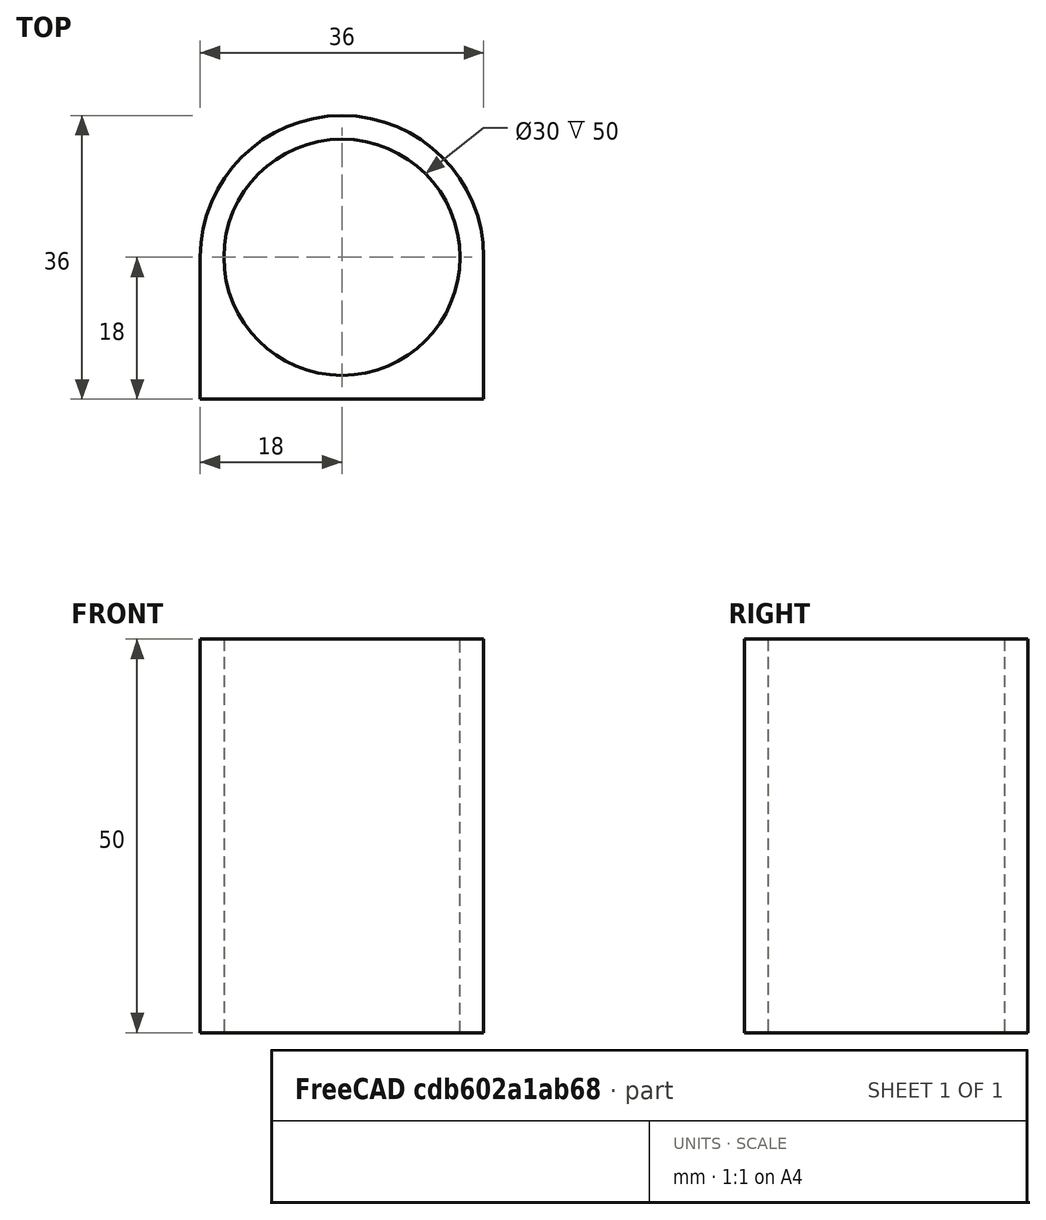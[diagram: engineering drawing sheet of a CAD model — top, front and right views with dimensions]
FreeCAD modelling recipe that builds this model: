
FCSTD DOCUMENT  (FreeCAD 0.19R24276 (Git))
Label: Cilinder_Sq
License: All rights reserved
LicenseURL: http://en.wikipedia.org/wiki/All_rights_reserved
objects: Sketcher::SketchObject×1, PartDesign::Pad×1, PartDesign::Body×1
note: 4 computed .brp shape members not serialized (recipe doc carries the construction recipe); baked Part::Feature solids carry a one-line shape summary decoded from their .brp

FEATURE [Sketcher::SketchObject] Sketch
  FullyConstrained = false
  MapMode = 5
  Support = -> [XY_Plane]
  sketch-geometry (5):
    g0: ArcOfCircle CenterX=0 CenterY=0 CenterZ=0 NormalX=0 NormalY=0 NormalZ=1 AngleXU=0 Radius=18 StartAngle=0 EndAngle=3.14159
    g1: Circle CenterX=0 CenterY=0 CenterZ=0 NormalX=0 NormalY=0 NormalZ=1 AngleXU=0 Radius=15
    g2: LineSegment StartX=18 StartY=0 StartZ=0 EndX=18 EndY=-18 EndZ=0
    g3: LineSegment StartX=18 StartY=-18 StartZ=0 EndX=-18 EndY=-18 EndZ=0
    g4: LineSegment StartX=-18 StartY=-18 StartZ=0 EndX=-18 EndY=0 EndZ=0
  constraints (9):
    c: Coincident(g0,g-1)
    c: Coincident(g1,g0)
    c: Diameter(g1) = 30
    c: Diameter(g0) = 36
    c: Coincident(g2,g3)
    c: Coincident(g3,g4)
    c: Horizontal(g3)
    c: Vertical(g2)
    c: Vertical(g4)
FEATURE [PartDesign::Pad] Pad
  Direction = (1,1,1)
  Length = 50
  Length2 = 100
  Profile = -> Sketch
  Type = 0
FEATURE [PartDesign::Body] Body  label="Body_cilinder_Sq"
  Group = -> [Sketch,Pad]
  Origin = -> Origin
  Tip = -> Pad
